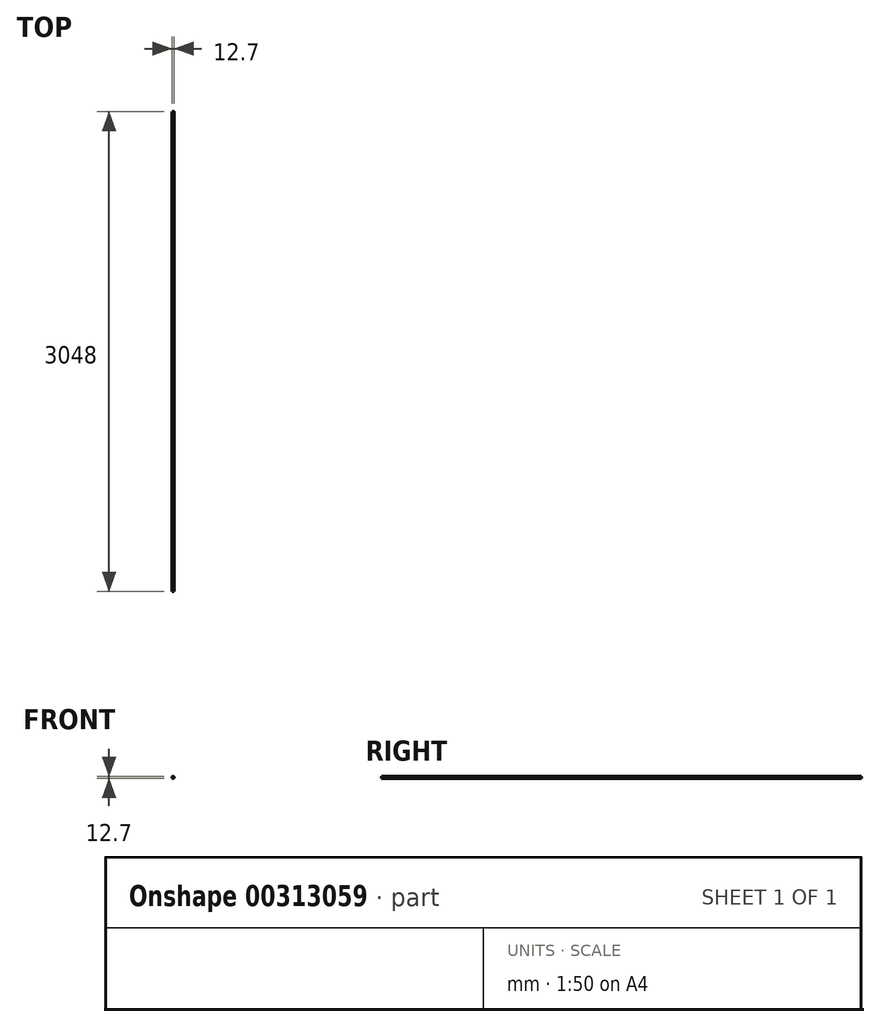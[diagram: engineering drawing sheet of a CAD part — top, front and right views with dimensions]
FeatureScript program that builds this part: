
annotation { "Feature Type Name" : "Feature", "Feature Type Description" : "" }
export const myFeature = defineFeature(function(context is Context, id is Id, definition is map)
    precondition{}
    {
        {
            var Q0;
            Q0=qCreatedBy(makeId("Front.planeOp"),FACE);
            var sketch = newSketch(context, id + "F0", { "sketchPlane" : qUnion([Q0])});
            skCircle(sketch, "E0", {"center": v(-37.65, 27.24) * mm, "radius": 6.35 * mm});
            skSolve(sketch);
        }
        {
            var Q0;
            Q0=makeQuery(id+"F0.imprint","IMPRINT",FACE,{"disambiguationData":[TD([[makeQuery(id+"F0.imprint","IMPRINT",EDGE,{"derivedFrom":sQuery(id+"F0.wireOp",EDGE,"E0")}),1.0]])]});
            extrude(context, id + "F1", {"entities" : qUnion([Q0]), "depth" : 3048 * mm});
        }
    });
